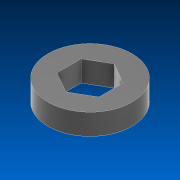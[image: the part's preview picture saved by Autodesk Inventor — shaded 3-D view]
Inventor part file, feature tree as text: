
AUTODESK INVENTOR PART (.ipt)
format: ipt  version: 2022.2 (Build 262287000, 287)  size: 93,696 bytes
history: native  units: in
note: dims shown in document units (in); Inventor stores cm internally (conversion verified against a paired STEP export)
features: extrude x1, sketch x1
ambient origin geometry x8: Origin, YZ Plane, XZ Plane, XY Plane, X Axis, Y Axis, Z Axis, Center Point
bodies: Solid1 (feature_tree)
feature tree (2):
  extrude  "Extrusion1"  Depth=0.125in
  sketch  "Sketch1"  dims[d0=0.25in d1=0.5in d2=0.125in d3=0.0in]
